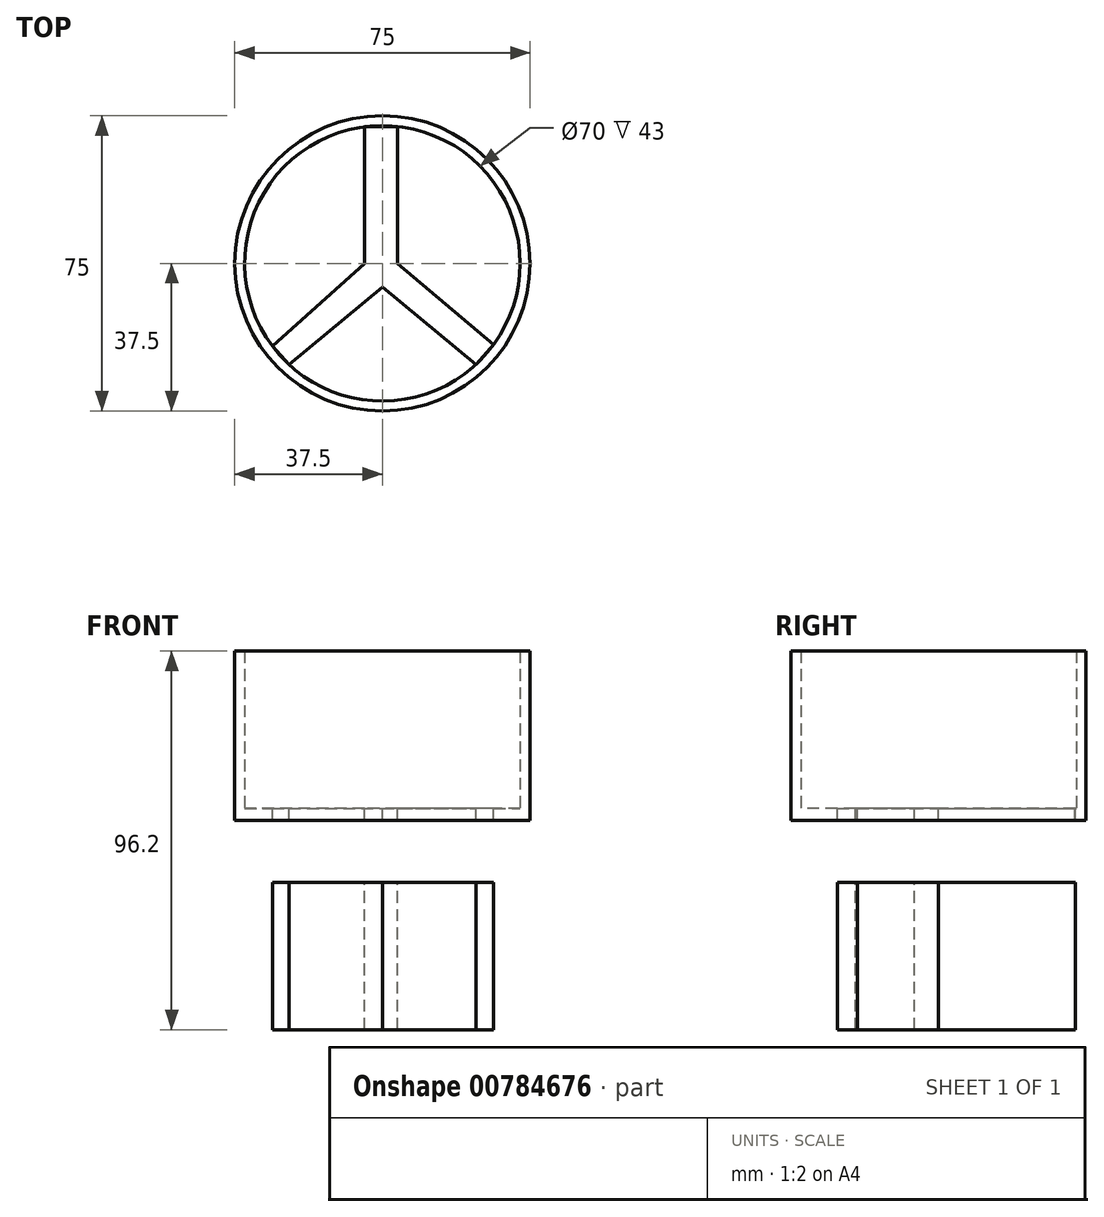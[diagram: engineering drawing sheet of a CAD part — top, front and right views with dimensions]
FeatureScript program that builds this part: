
annotation { "Feature Type Name" : "Feature", "Feature Type Description" : "" }
export const myFeature = defineFeature(function(context is Context, id is Id, definition is map)
    precondition{}
    {
        {
            var Q0;
            Q0=qCreatedBy(makeId("Top.planeOp"),FACE);
            var sketch = newSketch(context, id + "F0", { "sketchPlane" : qUnion([Q0])});
            skCircle(sketch, "E0", {"center": v(0, 0) * mm, "radius": 37.5 * mm});
            skSolve(sketch);
        }
        {
            var Q0;
            Q0=qSketchRegion(id+"F0",true);
            extrude(context, id + "F1", {"entities" : qUnion([Q0]), "depth" : 3 * mm, "offsetDistance" : 25 * mm});
        }
        {
            var Q0;
            Q0=makeQuery(id+"F1.opExtrude","CAP_FACE",FACE,{"disambiguationData":[OSD([sQuery(id+"F0.wireOp",EDGE,"E0")])],"isStart":false});
            var sketch = newSketch(context, id + "F2", { "sketchPlane" : qUnion([Q0])});
            skCircle(sketch, "E1", {"center": v(0, 0) * mm, "radius": 35 * mm});
            skCircle(sketch, "E2.0", {"center": v(0, 0) * mm, "radius": 37.5 * mm});
            skSolve(sketch);
        }
        {
            var Q0;
            Q0=makeQuery(id+"F2.imprint","IMPRINT",FACE,{"disambiguationData":[TD([[makeQuery(id+"F2.imprint","IMPRINT",EDGE,{"derivedFrom":sQuery(id+"F2.wireOp",EDGE,"E1")}),-1.0]])]});
            extrude(context, id + "F3", {"entities" : qUnion([Q0]), "operationType" : NewBodyOperationType.ADD, "depth" : 40 * mm, "offsetDistance" : 25 * mm});
        }
        {
            var Q0;
            Q0=makeQuery(id+"F1.opExtrude","CAP_FACE",FACE,{"disambiguationData":[OSD([sQuery(id+"F0.wireOp",EDGE,"E0")])],"isStart":false});
            var sketch = newSketch(context, id + "F4", { "sketchPlane" : qUnion([Q0])});
            skLineSegment(sketch, "E3", {"start": v(-4.54, 34.7) * mm, "end": v(-4.54, 5.52) * mm});
            skLineSegment(sketch, "E4", {"start": v(-4.54, 5.52) * mm, "end": v(-4.54, 0) * mm});
            skLineSegment(sketch, "E5", {"start": v(-4.54, 0) * mm, "end": v(-27.95, -21.07) * mm});
            skLineSegment(sketch, "E6", {"start": v(-27.95, -21.07) * mm, "end": v(-23.73, -25.72) * mm});
            skLineSegment(sketch, "E7", {"start": v(-23.73, -25.72) * mm, "end": v(0, -6.1) * mm});
            skLineSegment(sketch, "E8", {"start": v(0, -6.1) * mm, "end": v(23.73, -25.72) * mm});
            skLineSegment(sketch, "E9", {"start": v(23.73, -25.72) * mm, "end": v(28.29, -20.61) * mm});
            skLineSegment(sketch, "E10", {"start": v(28.29, -20.61) * mm, "end": v(3.82, 0) * mm});
            skLineSegment(sketch, "E11", {"start": v(3.82, 0) * mm, "end": v(3.82, 34.8) * mm});
            skLineSegment(sketch, "E12", {"start": v(3.82, 34.8) * mm, "end": v(-4.54, 34.7) * mm});
            skSolve(sketch);
        }
        {
            var Q0;
            Q0=makeQuery(id+"F4.imprint","IMPRINT",FACE,{"disambiguationData":[TD([[makeQuery(id+"F4.imprint","IMPRINT",EDGE,{"derivedFrom":sQuery(id+"F4.wireOp",EDGE,"E3")}),1.0]])]});
            extrude(context, id + "F5", {"entities" : qUnion([Q0]), "operationType" : NewBodyOperationType.ADD, "oppositeDirection" : true, "depth" : 56.2 * mm, "offsetDistance" : 25 * mm});
        }
        {
            var Q0;
            {var subQ0=sQuery(id+"F4.wireOp",EDGE,"E9");Q0=makeQuery(id+"F4.imprint","IMPRINT",FACE,{"disambiguationData":[TD([[makeQuery(id+"F4.imprint","IMPRINT",EDGE,{"derivedFrom":subQ0}),-1.0]])]});}
            var Q1;
            Q1=makeQuery(id+"F4.imprint","IMPRINT",FACE,{"disambiguationData":[TD([[makeQuery(id+"F4.imprint","IMPRINT",EDGE,{"derivedFrom":sQuery(id+"F4.wireOp",EDGE,"E3")}),1.0]])]});
            extrude(context, id + "F6", {"entities" : qUnion([Q0, Q1]), "operationType" : NewBodyOperationType.REMOVE, "oppositeDirection" : true, "depth" : 18.8 * mm, "offsetDistance" : 25 * mm});
        }
    });
